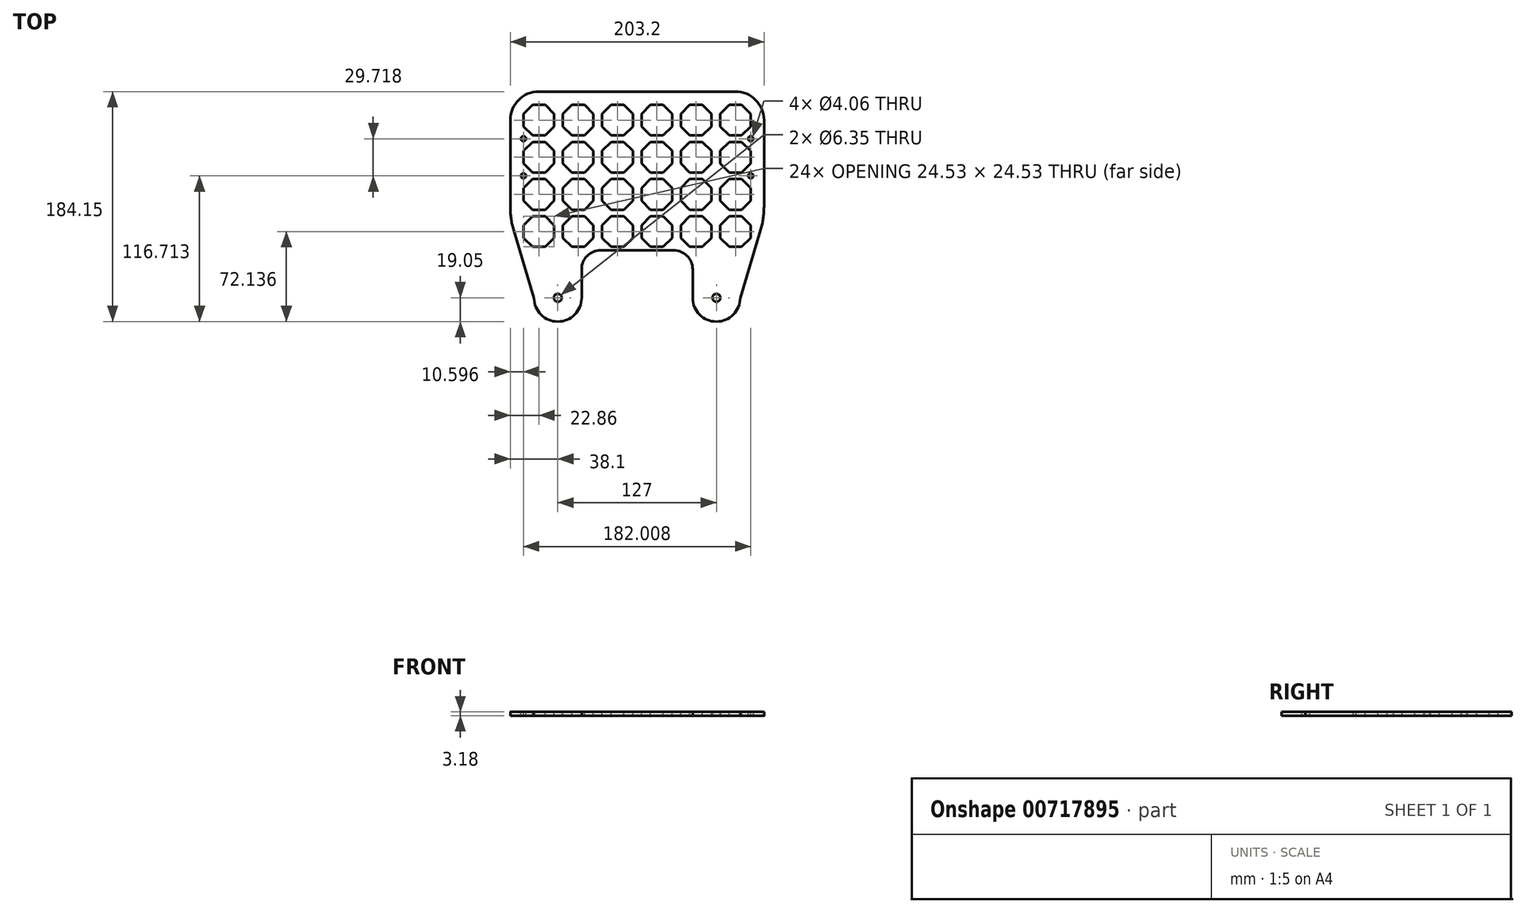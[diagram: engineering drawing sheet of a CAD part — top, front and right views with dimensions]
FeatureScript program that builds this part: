
annotation { "Feature Type Name" : "Feature", "Feature Type Description" : "" }
export const myFeature = defineFeature(function(context is Context, id is Id, definition is map)
    precondition{}
    {
        {
            var Q0;
            Q0=qCreatedBy(makeId("Top.planeOp"),FACE);
            var sketch = newSketch(context, id + "F0", { "sketchPlane" : qUnion([Q0])});
            skLineSegment(sketch, "E0.bottom", {"start": v(111.62, -50.8) * mm, "end": v(-91.58, -50.8) * mm});
            skLineSegment(sketch, "E0.top", {"start": v(88.76, 50.8) * mm, "end": v(-68.72, 50.8) * mm});
            skLineSegment(sketch, "E0.left", {"start": v(111.62, -41.48) * mm, "end": v(111.62, 27.94) * mm});
            skLineSegment(sketch, "E0.right", {"start": v(-91.58, -41.48) * mm, "end": v(-91.58, 27.94) * mm});
            skPoint(sketch, "E0.middle", {"position": v(10.02, 0) * mm});
            skLineSegment(sketch, "E1.bottom", {"start": v(-91.58, -50.8) * mm, "end": v(111.62, -50.8) * mm});
            skLineSegment(sketch, "E1.top", {"start": v(-19.19, -76.2) * mm, "end": v(39.23, -76.2) * mm});
            skLineSegment(sketch, "E2.bottom", {"start": v(54.47, -76.2) * mm, "end": v(92.57, -76.2) * mm});
            skLineSegment(sketch, "E2.top", {"start": v(54.47, -114.3) * mm, "end": v(92.57, -114.3) * mm});
            skLineSegment(sketch, "E2.left", {"start": v(54.47, -91.44) * mm, "end": v(54.47, -114.3) * mm});
            skLineSegment(sketch, "E2.right", {"start": v(92.57, -76.2) * mm, "end": v(92.57, -114.3) * mm});
            skPoint(sketch, "E3.oppositeSnap0", {"position": v(73.52, -114.3) * mm});
            skLineSegment(sketch, "E3.bottom", {"start": v(-72.53, -76.2) * mm, "end": v(-34.43, -76.2) * mm});
            skLineSegment(sketch, "E3.top", {"start": v(-72.53, -114.3) * mm, "end": v(-34.43, -114.3) * mm});
            skLineSegment(sketch, "E3.left", {"start": v(-72.53, -76.2) * mm, "end": v(-72.53, -114.3) * mm});
            skLineSegment(sketch, "E3.right", {"start": v(-34.43, -91.44) * mm, "end": v(-34.43, -114.3) * mm});
            skCircle(sketch, "E4", {"center": v(73.52, -114.3) * mm, "radius": 19.05 * mm});
            skCircle(sketch, "E5", {"center": v(-53.48, -114.3) * mm, "radius": 19.05 * mm});
            skLineSegment(sketch, "E6", {"start": v(-88.9, -59.73) * mm, "end": v(-72.53, -114.3) * mm});
            skLineSegment(sketch, "E7", {"start": v(108.94, -59.73) * mm, "end": v(92.57, -114.3) * mm});
            skPoint(sketch, "E1.left.end.orphan", {"position": v(-91.58, -76.2) * mm});
            skPoint(sketch, "E8.orphan", {"position": v(111.62, -76.2) * mm});
            skPoint(sketch, "E9.visualSharp", {"position": v(-91.58, 50.8) * mm});
            skArc(sketch, "E9.filletArc", {"start": v(-68.72, 50.8) * mm, "mid": v(-84.88, 44.1) * mm, "end": v(-91.58, 27.94) * mm});
            skPoint(sketch, "E10.visualSharp", {"position": v(111.62, 50.8) * mm});
            skArc(sketch, "E10.filletArc", {"start": v(111.62, 27.94) * mm, "mid": v(104.92, 44.1) * mm, "end": v(88.76, 50.8) * mm});
            skPoint(sketch, "E11.visualSharp", {"position": v(-91.58, -50.8) * mm});
            skArc(sketch, "E11.filletArc", {"start": v(-91.58, -41.48) * mm, "mid": v(-90.9, -50.7) * mm, "end": v(-88.9, -59.73) * mm});
            skPoint(sketch, "E12.visualSharp", {"position": v(111.62, -50.8) * mm});
            skArc(sketch, "E12.filletArc", {"start": v(108.94, -59.73) * mm, "mid": v(110.95, -50.7) * mm, "end": v(111.62, -41.48) * mm});
            skCircle(sketch, "E13", {"center": v(-53.48, -114.3) * mm, "radius": 3.18 * mm});
            skCircle(sketch, "E14", {"center": v(73.52, -114.3) * mm, "radius": 3.18 * mm});
            skPoint(sketch, "E15.newPointA", {"position": v(-34.43, -76.2) * mm});
            skArc(sketch, "E15.filletArc", {"start": v(-19.19, -76.2) * mm, "mid": v(-29.97, -80.66) * mm, "end": v(-34.43, -91.44) * mm});
            skPoint(sketch, "E16.newPointB", {"position": v(54.47, -76.2) * mm});
            skArc(sketch, "E16.filletArc", {"start": v(54.47, -91.44) * mm, "mid": v(50, -80.66) * mm, "end": v(39.23, -76.2) * mm});
            skSolve(sketch);
        }
        {
            var Q0;
            Q0=qSketchRegion(id+"F0",true);
            extrude(context, id + "F1", {"entities" : qUnion([Q0]), "depth" : 3.17 * mm, "offsetDistance" : 25.4 * mm});
        }
        {
            var Q0;
            Q0=makeQuery(id+"F1.opExtrude","CAP_FACE",FACE,{"disambiguationData":[OSD([sQuery(id+"F0.wireOp",EDGE,"E0.top"),sQuery(id+"F0.wireOp",EDGE,"E0.left"),sQuery(id+"F0.wireOp",EDGE,"E0.right"),sQuery(id+"F0.wireOp",EDGE,"E1.top"),sQuery(id+"F0.wireOp",EDGE,"E2.left"),sQuery(id+"F0.wireOp",EDGE,"E3.right"),sQuery(id+"F0.wireOp",EDGE,"E4"),sQuery(id+"F0.wireOp",EDGE,"E5"),sQuery(id+"F0.wireOp",EDGE,"E6"),sQuery(id+"F0.wireOp",EDGE,"E7"),sQuery(id+"F0.wireOp",EDGE,"E9.filletArc"),sQuery(id+"F0.wireOp",EDGE,"E10.filletArc"),sQuery(id+"F0.wireOp",EDGE,"E11.filletArc"),sQuery(id+"F0.wireOp",EDGE,"E12.filletArc"),sQuery(id+"F0.wireOp",EDGE,"E13"),sQuery(id+"F0.wireOp",EDGE,"E14"),sQuery(id+"F0.wireOp",EDGE,"E15.filletArc"),sQuery(id+"F0.wireOp",EDGE,"E16.filletArc")])],"isStart":false});
            var sketch = newSketch(context, id + "F2", { "sketchPlane" : qUnion([Q0])});
            skCircle(sketch, "E17.cCircle", {"center": v(-68.72, 27.94) * mm, "radius": 12.26 * mm, "construction": true});
            skLineSegment(sketch, "E17.0", {"start": v(-73.8, 40.2) * mm, "end": v(-63.64, 40.2) * mm});
            skLineSegment(sketch, "E17.1", {"start": v(-63.64, 40.2) * mm, "end": v(-56.46, 33.02) * mm});
            skLineSegment(sketch, "E17.2", {"start": v(-56.46, 33.02) * mm, "end": v(-56.46, 22.86) * mm});
            skLineSegment(sketch, "E17.3", {"start": v(-56.46, 22.86) * mm, "end": v(-63.64, 15.68) * mm});
            skLineSegment(sketch, "E17.4", {"start": v(-63.64, 15.68) * mm, "end": v(-73.8, 15.68) * mm});
            skLineSegment(sketch, "E17.5", {"start": v(-73.8, 15.68) * mm, "end": v(-80.98, 22.86) * mm});
            skLineSegment(sketch, "E17.6", {"start": v(-80.98, 22.86) * mm, "end": v(-80.98, 33.02) * mm});
            skLineSegment(sketch, "E17.7", {"start": v(-80.98, 33.02) * mm, "end": v(-73.8, 40.2) * mm});
            skPoint(sketch, "E17.0.midPoint", {"position": v(-68.72, 40.2) * mm});
            skLineSegment(sketch, "E18", {"start": v(10.02, 50.8) * mm, "end": v(10.02, -76.2) * mm, "construction": true});
            skLineSegment(sketch, "E19.0.1.0", {"start": v(-63.64, -14.04) * mm, "end": v(-73.8, -14.04) * mm});
            skLineSegment(sketch, "E19.0.1.1", {"start": v(-73.8, -14.04) * mm, "end": v(-80.98, -6.86) * mm});
            skLineSegment(sketch, "E19.0.1.2", {"start": v(-80.98, -6.86) * mm, "end": v(-80.98, 3.3) * mm});
            skLineSegment(sketch, "E19.0.1.3", {"start": v(-80.98, 3.3) * mm, "end": v(-73.8, 10.49) * mm});
            skLineSegment(sketch, "E19.0.1.4", {"start": v(-73.8, 10.49) * mm, "end": v(-63.64, 10.49) * mm});
            skLineSegment(sketch, "E19.0.1.5", {"start": v(-63.64, 10.49) * mm, "end": v(-56.46, 3.3) * mm});
            skLineSegment(sketch, "E19.0.1.6", {"start": v(-56.46, 3.3) * mm, "end": v(-56.46, -6.86) * mm});
            skLineSegment(sketch, "E19.0.1.7", {"start": v(-56.46, -6.86) * mm, "end": v(-63.64, -14.04) * mm});
            skLineSegment(sketch, "E19.0.2.0", {"start": v(-63.64, -43.76) * mm, "end": v(-73.8, -43.76) * mm});
            skLineSegment(sketch, "E19.0.2.1", {"start": v(-73.8, -43.76) * mm, "end": v(-80.98, -36.58) * mm});
            skLineSegment(sketch, "E19.0.2.2", {"start": v(-80.98, -36.58) * mm, "end": v(-80.98, -26.42) * mm});
            skLineSegment(sketch, "E19.0.2.3", {"start": v(-80.98, -26.42) * mm, "end": v(-73.8, -19.23) * mm});
            skLineSegment(sketch, "E19.0.2.4", {"start": v(-73.8, -19.23) * mm, "end": v(-63.64, -19.23) * mm});
            skLineSegment(sketch, "E19.0.2.5", {"start": v(-63.64, -19.23) * mm, "end": v(-56.46, -26.42) * mm});
            skLineSegment(sketch, "E19.0.2.6", {"start": v(-56.46, -26.42) * mm, "end": v(-56.46, -36.58) * mm});
            skLineSegment(sketch, "E19.0.2.7", {"start": v(-56.46, -36.58) * mm, "end": v(-63.64, -43.76) * mm});
            skLineSegment(sketch, "E19.0.3.0", {"start": v(-63.64, -73.48) * mm, "end": v(-73.8, -73.48) * mm});
            skLineSegment(sketch, "E19.0.3.1", {"start": v(-73.8, -73.48) * mm, "end": v(-80.98, -66.3) * mm});
            skLineSegment(sketch, "E19.0.3.2", {"start": v(-80.98, -66.3) * mm, "end": v(-80.98, -56.13) * mm});
            skLineSegment(sketch, "E19.0.3.3", {"start": v(-80.98, -56.13) * mm, "end": v(-73.8, -48.95) * mm});
            skLineSegment(sketch, "E19.0.3.4", {"start": v(-73.8, -48.95) * mm, "end": v(-63.64, -48.95) * mm});
            skLineSegment(sketch, "E19.0.3.5", {"start": v(-63.64, -48.95) * mm, "end": v(-56.46, -56.13) * mm});
            skLineSegment(sketch, "E19.0.3.6", {"start": v(-56.46, -56.13) * mm, "end": v(-56.46, -66.3) * mm});
            skLineSegment(sketch, "E19.0.3.7", {"start": v(-56.46, -66.3) * mm, "end": v(-63.64, -73.48) * mm});
            skLineSegment(sketch, "E19.1.0.0", {"start": v(-32.14, 15.68) * mm, "end": v(-42.3, 15.68) * mm});
            skLineSegment(sketch, "E19.1.0.1", {"start": v(-42.3, 15.68) * mm, "end": v(-49.49, 22.86) * mm});
            skLineSegment(sketch, "E19.1.0.2", {"start": v(-49.49, 22.86) * mm, "end": v(-49.49, 33.02) * mm});
            skLineSegment(sketch, "E19.1.0.3", {"start": v(-49.49, 33.02) * mm, "end": v(-42.3, 40.2) * mm});
            skLineSegment(sketch, "E19.1.0.4", {"start": v(-42.3, 40.2) * mm, "end": v(-32.14, 40.2) * mm});
            skLineSegment(sketch, "E19.1.0.5", {"start": v(-32.14, 40.2) * mm, "end": v(-24.96, 33.02) * mm});
            skLineSegment(sketch, "E19.1.0.6", {"start": v(-24.96, 33.02) * mm, "end": v(-24.96, 22.86) * mm});
            skLineSegment(sketch, "E19.1.0.7", {"start": v(-24.96, 22.86) * mm, "end": v(-32.14, 15.68) * mm});
            skLineSegment(sketch, "E19.1.1.0", {"start": v(-32.14, -14.04) * mm, "end": v(-42.3, -14.04) * mm});
            skLineSegment(sketch, "E19.1.1.1", {"start": v(-42.3, -14.04) * mm, "end": v(-49.49, -6.86) * mm});
            skLineSegment(sketch, "E19.1.1.2", {"start": v(-49.49, -6.86) * mm, "end": v(-49.49, 3.3) * mm});
            skLineSegment(sketch, "E19.1.1.3", {"start": v(-49.49, 3.3) * mm, "end": v(-42.3, 10.49) * mm});
            skLineSegment(sketch, "E19.1.1.4", {"start": v(-42.3, 10.49) * mm, "end": v(-32.14, 10.49) * mm});
            skLineSegment(sketch, "E19.1.1.5", {"start": v(-32.14, 10.49) * mm, "end": v(-24.96, 3.3) * mm});
            skLineSegment(sketch, "E19.1.1.6", {"start": v(-24.96, 3.3) * mm, "end": v(-24.96, -6.86) * mm});
            skLineSegment(sketch, "E19.1.1.7", {"start": v(-24.96, -6.86) * mm, "end": v(-32.14, -14.04) * mm});
            skLineSegment(sketch, "E19.1.2.0", {"start": v(-32.14, -43.76) * mm, "end": v(-42.3, -43.76) * mm});
            skLineSegment(sketch, "E19.1.2.1", {"start": v(-42.3, -43.76) * mm, "end": v(-49.49, -36.58) * mm});
            skLineSegment(sketch, "E19.1.2.2", {"start": v(-49.49, -36.58) * mm, "end": v(-49.49, -26.42) * mm});
            skLineSegment(sketch, "E19.1.2.3", {"start": v(-49.49, -26.42) * mm, "end": v(-42.3, -19.23) * mm});
            skLineSegment(sketch, "E19.1.2.4", {"start": v(-42.3, -19.23) * mm, "end": v(-32.14, -19.23) * mm});
            skLineSegment(sketch, "E19.1.2.5", {"start": v(-32.14, -19.23) * mm, "end": v(-24.96, -26.42) * mm});
            skLineSegment(sketch, "E19.1.2.6", {"start": v(-24.96, -26.42) * mm, "end": v(-24.96, -36.58) * mm});
            skLineSegment(sketch, "E19.1.2.7", {"start": v(-24.96, -36.58) * mm, "end": v(-32.14, -43.76) * mm});
            skLineSegment(sketch, "E19.1.3.0", {"start": v(-32.14, -73.48) * mm, "end": v(-42.3, -73.48) * mm});
            skLineSegment(sketch, "E19.1.3.1", {"start": v(-42.3, -73.48) * mm, "end": v(-49.49, -66.3) * mm});
            skLineSegment(sketch, "E19.1.3.2", {"start": v(-49.49, -66.3) * mm, "end": v(-49.49, -56.13) * mm});
            skLineSegment(sketch, "E19.1.3.3", {"start": v(-49.49, -56.13) * mm, "end": v(-42.3, -48.95) * mm});
            skLineSegment(sketch, "E19.1.3.4", {"start": v(-42.3, -48.95) * mm, "end": v(-32.14, -48.95) * mm});
            skLineSegment(sketch, "E19.1.3.5", {"start": v(-32.14, -48.95) * mm, "end": v(-24.96, -56.13) * mm});
            skLineSegment(sketch, "E19.1.3.6", {"start": v(-24.96, -56.13) * mm, "end": v(-24.96, -66.3) * mm});
            skLineSegment(sketch, "E19.1.3.7", {"start": v(-24.96, -66.3) * mm, "end": v(-32.14, -73.48) * mm});
            skLineSegment(sketch, "E19.2.0.0", {"start": v(-0.65, 15.68) * mm, "end": v(-10.8, 15.68) * mm});
            skLineSegment(sketch, "E19.2.0.1", {"start": v(-10.8, 15.68) * mm, "end": v(-18, 22.86) * mm});
            skLineSegment(sketch, "E19.2.0.2", {"start": v(-18, 22.86) * mm, "end": v(-18, 33.02) * mm});
            skLineSegment(sketch, "E19.2.0.3", {"start": v(-18, 33.02) * mm, "end": v(-10.8, 40.2) * mm});
            skLineSegment(sketch, "E19.2.0.4", {"start": v(-10.8, 40.2) * mm, "end": v(-0.65, 40.2) * mm});
            skLineSegment(sketch, "E19.2.0.5", {"start": v(-0.65, 40.2) * mm, "end": v(6.54, 33.02) * mm});
            skLineSegment(sketch, "E19.2.0.6", {"start": v(6.54, 33.02) * mm, "end": v(6.54, 22.86) * mm});
            skLineSegment(sketch, "E19.2.0.7", {"start": v(6.54, 22.86) * mm, "end": v(-0.65, 15.68) * mm});
            skLineSegment(sketch, "E19.2.1.0", {"start": v(-0.65, -14.04) * mm, "end": v(-10.8, -14.04) * mm});
            skLineSegment(sketch, "E19.2.1.1", {"start": v(-10.8, -14.04) * mm, "end": v(-18, -6.86) * mm});
            skLineSegment(sketch, "E19.2.1.2", {"start": v(-18, -6.86) * mm, "end": v(-18, 3.3) * mm});
            skLineSegment(sketch, "E19.2.1.3", {"start": v(-18, 3.3) * mm, "end": v(-10.8, 10.49) * mm});
            skLineSegment(sketch, "E19.2.1.4", {"start": v(-10.8, 10.49) * mm, "end": v(-0.65, 10.49) * mm});
            skLineSegment(sketch, "E19.2.1.5", {"start": v(-0.65, 10.49) * mm, "end": v(6.54, 3.3) * mm});
            skLineSegment(sketch, "E19.2.1.6", {"start": v(6.54, 3.3) * mm, "end": v(6.54, -6.86) * mm});
            skLineSegment(sketch, "E19.2.1.7", {"start": v(6.54, -6.86) * mm, "end": v(-0.65, -14.04) * mm});
            skLineSegment(sketch, "E19.2.2.0", {"start": v(-0.65, -43.76) * mm, "end": v(-10.8, -43.76) * mm});
            skLineSegment(sketch, "E19.2.2.1", {"start": v(-10.8, -43.76) * mm, "end": v(-18, -36.58) * mm});
            skLineSegment(sketch, "E19.2.2.2", {"start": v(-18, -36.58) * mm, "end": v(-18, -26.42) * mm});
            skLineSegment(sketch, "E19.2.2.3", {"start": v(-18, -26.42) * mm, "end": v(-10.8, -19.23) * mm});
            skLineSegment(sketch, "E19.2.2.4", {"start": v(-10.8, -19.23) * mm, "end": v(-0.65, -19.23) * mm});
            skLineSegment(sketch, "E19.2.2.5", {"start": v(-0.65, -19.23) * mm, "end": v(6.54, -26.42) * mm});
            skLineSegment(sketch, "E19.2.2.6", {"start": v(6.54, -26.42) * mm, "end": v(6.54, -36.58) * mm});
            skLineSegment(sketch, "E19.2.2.7", {"start": v(6.54, -36.58) * mm, "end": v(-0.65, -43.76) * mm});
            skLineSegment(sketch, "E19.2.3.0", {"start": v(-0.65, -73.48) * mm, "end": v(-10.8, -73.48) * mm});
            skLineSegment(sketch, "E19.2.3.1", {"start": v(-10.8, -73.48) * mm, "end": v(-18, -66.3) * mm});
            skLineSegment(sketch, "E19.2.3.2", {"start": v(-18, -66.3) * mm, "end": v(-18, -56.13) * mm});
            skLineSegment(sketch, "E19.2.3.3", {"start": v(-18, -56.13) * mm, "end": v(-10.8, -48.95) * mm});
            skLineSegment(sketch, "E19.2.3.4", {"start": v(-10.8, -48.95) * mm, "end": v(-0.65, -48.95) * mm});
            skLineSegment(sketch, "E19.2.3.5", {"start": v(-0.65, -48.95) * mm, "end": v(6.54, -56.13) * mm});
            skLineSegment(sketch, "E19.2.3.6", {"start": v(6.54, -56.13) * mm, "end": v(6.54, -66.3) * mm});
            skLineSegment(sketch, "E19.2.3.7", {"start": v(6.54, -66.3) * mm, "end": v(-0.65, -73.48) * mm});
            skLineSegment(sketch, "E19.direction1", {"start": v(-73.8, 15.68) * mm, "end": v(-42.3, 15.68) * mm, "construction": true});
            skLineSegment(sketch, "E19.direction2", {"start": v(-73.8, 15.68) * mm, "end": v(-73.8, -14.04) * mm, "construction": true});
            skLineSegment(sketch, "E20.0.3.0", {"start": v(30.85, 15.68) * mm, "end": v(20.69, 15.68) * mm});
            skLineSegment(sketch, "E20.3.3.0", {"start": v(20.69, 15.68) * mm, "end": v(13.5, 22.86) * mm});
            skLineSegment(sketch, "E20.6.3.0", {"start": v(13.5, 22.86) * mm, "end": v(13.5, 33.02) * mm});
            skLineSegment(sketch, "E20.9.3.0", {"start": v(13.5, 33.02) * mm, "end": v(20.69, 40.2) * mm});
            skLineSegment(sketch, "E20.12.3.0", {"start": v(20.69, 40.2) * mm, "end": v(30.85, 40.2) * mm});
            skLineSegment(sketch, "E20.15.3.0", {"start": v(30.85, 40.2) * mm, "end": v(38.03, 33.02) * mm});
            skLineSegment(sketch, "E20.18.3.0", {"start": v(38.03, 33.02) * mm, "end": v(38.03, 22.86) * mm});
            skLineSegment(sketch, "E20.21.3.0", {"start": v(38.03, 22.86) * mm, "end": v(30.85, 15.68) * mm});
            skLineSegment(sketch, "E20.0.3.1", {"start": v(30.85, -14.04) * mm, "end": v(20.69, -14.04) * mm});
            skLineSegment(sketch, "E20.3.3.1", {"start": v(20.69, -14.04) * mm, "end": v(13.5, -6.86) * mm});
            skLineSegment(sketch, "E20.6.3.1", {"start": v(13.5, -6.86) * mm, "end": v(13.5, 3.3) * mm});
            skLineSegment(sketch, "E20.9.3.1", {"start": v(13.5, 3.3) * mm, "end": v(20.69, 10.49) * mm});
            skLineSegment(sketch, "E20.12.3.1", {"start": v(20.69, 10.49) * mm, "end": v(30.85, 10.49) * mm});
            skLineSegment(sketch, "E20.15.3.1", {"start": v(30.85, 10.49) * mm, "end": v(38.03, 3.3) * mm});
            skLineSegment(sketch, "E20.18.3.1", {"start": v(38.03, 3.3) * mm, "end": v(38.03, -6.86) * mm});
            skLineSegment(sketch, "E20.21.3.1", {"start": v(38.03, -6.86) * mm, "end": v(30.85, -14.04) * mm});
            skLineSegment(sketch, "E20.0.3.2", {"start": v(30.85, -43.76) * mm, "end": v(20.69, -43.76) * mm});
            skLineSegment(sketch, "E20.3.3.2", {"start": v(20.69, -43.76) * mm, "end": v(13.5, -36.58) * mm});
            skLineSegment(sketch, "E20.6.3.2", {"start": v(13.5, -36.58) * mm, "end": v(13.5, -26.42) * mm});
            skLineSegment(sketch, "E20.9.3.2", {"start": v(13.5, -26.42) * mm, "end": v(20.69, -19.23) * mm});
            skLineSegment(sketch, "E20.12.3.2", {"start": v(20.69, -19.23) * mm, "end": v(30.85, -19.23) * mm});
            skLineSegment(sketch, "E20.15.3.2", {"start": v(30.85, -19.23) * mm, "end": v(38.03, -26.42) * mm});
            skLineSegment(sketch, "E20.18.3.2", {"start": v(38.03, -26.42) * mm, "end": v(38.03, -36.58) * mm});
            skLineSegment(sketch, "E20.21.3.2", {"start": v(38.03, -36.58) * mm, "end": v(30.85, -43.76) * mm});
            skLineSegment(sketch, "E20.0.3.3", {"start": v(30.85, -73.48) * mm, "end": v(20.69, -73.48) * mm});
            skLineSegment(sketch, "E20.3.3.3", {"start": v(20.69, -73.48) * mm, "end": v(13.5, -66.3) * mm});
            skLineSegment(sketch, "E20.6.3.3", {"start": v(13.5, -66.3) * mm, "end": v(13.5, -56.13) * mm});
            skLineSegment(sketch, "E20.9.3.3", {"start": v(13.5, -56.13) * mm, "end": v(20.69, -48.95) * mm});
            skLineSegment(sketch, "E20.12.3.3", {"start": v(20.69, -48.95) * mm, "end": v(30.85, -48.95) * mm});
            skLineSegment(sketch, "E20.15.3.3", {"start": v(30.85, -48.95) * mm, "end": v(38.03, -56.13) * mm});
            skLineSegment(sketch, "E20.18.3.3", {"start": v(38.03, -56.13) * mm, "end": v(38.03, -66.3) * mm});
            skLineSegment(sketch, "E20.21.3.3", {"start": v(38.03, -66.3) * mm, "end": v(30.85, -73.48) * mm});
            skLineSegment(sketch, "E20.0.4.0", {"start": v(62.34, 15.68) * mm, "end": v(52.18, 15.68) * mm});
            skLineSegment(sketch, "E20.3.4.0", {"start": v(52.18, 15.68) * mm, "end": v(45, 22.86) * mm});
            skLineSegment(sketch, "E20.6.4.0", {"start": v(45, 22.86) * mm, "end": v(45, 33.02) * mm});
            skLineSegment(sketch, "E20.9.4.0", {"start": v(45, 33.02) * mm, "end": v(52.18, 40.2) * mm});
            skLineSegment(sketch, "E20.12.4.0", {"start": v(52.18, 40.2) * mm, "end": v(62.34, 40.2) * mm});
            skLineSegment(sketch, "E20.15.4.0", {"start": v(62.34, 40.2) * mm, "end": v(69.53, 33.02) * mm});
            skLineSegment(sketch, "E20.18.4.0", {"start": v(69.53, 33.02) * mm, "end": v(69.53, 22.86) * mm});
            skLineSegment(sketch, "E20.21.4.0", {"start": v(69.53, 22.86) * mm, "end": v(62.34, 15.68) * mm});
            skLineSegment(sketch, "E20.0.4.1", {"start": v(62.34, -14.04) * mm, "end": v(52.18, -14.04) * mm});
            skLineSegment(sketch, "E20.3.4.1", {"start": v(52.18, -14.04) * mm, "end": v(45, -6.86) * mm});
            skLineSegment(sketch, "E20.6.4.1", {"start": v(45, -6.86) * mm, "end": v(45, 3.3) * mm});
            skLineSegment(sketch, "E20.9.4.1", {"start": v(45, 3.3) * mm, "end": v(52.18, 10.49) * mm});
            skLineSegment(sketch, "E20.12.4.1", {"start": v(52.18, 10.49) * mm, "end": v(62.34, 10.49) * mm});
            skLineSegment(sketch, "E20.15.4.1", {"start": v(62.34, 10.49) * mm, "end": v(69.53, 3.3) * mm});
            skLineSegment(sketch, "E20.18.4.1", {"start": v(69.53, 3.3) * mm, "end": v(69.53, -6.86) * mm});
            skLineSegment(sketch, "E20.21.4.1", {"start": v(69.53, -6.86) * mm, "end": v(62.34, -14.04) * mm});
            skLineSegment(sketch, "E20.0.4.2", {"start": v(62.34, -43.76) * mm, "end": v(52.18, -43.76) * mm});
            skLineSegment(sketch, "E20.3.4.2", {"start": v(52.18, -43.76) * mm, "end": v(45, -36.58) * mm});
            skLineSegment(sketch, "E20.6.4.2", {"start": v(45, -36.58) * mm, "end": v(45, -26.42) * mm});
            skLineSegment(sketch, "E20.9.4.2", {"start": v(45, -26.42) * mm, "end": v(52.18, -19.23) * mm});
            skLineSegment(sketch, "E20.12.4.2", {"start": v(52.18, -19.23) * mm, "end": v(62.34, -19.23) * mm});
            skLineSegment(sketch, "E20.15.4.2", {"start": v(62.34, -19.23) * mm, "end": v(69.53, -26.42) * mm});
            skLineSegment(sketch, "E20.18.4.2", {"start": v(69.53, -26.42) * mm, "end": v(69.53, -36.58) * mm});
            skLineSegment(sketch, "E20.21.4.2", {"start": v(69.53, -36.58) * mm, "end": v(62.34, -43.76) * mm});
            skLineSegment(sketch, "E20.0.4.3", {"start": v(62.34, -73.48) * mm, "end": v(52.18, -73.48) * mm});
            skLineSegment(sketch, "E20.3.4.3", {"start": v(52.18, -73.48) * mm, "end": v(45, -66.3) * mm});
            skLineSegment(sketch, "E20.6.4.3", {"start": v(45, -66.3) * mm, "end": v(45, -56.13) * mm});
            skLineSegment(sketch, "E20.9.4.3", {"start": v(45, -56.13) * mm, "end": v(52.18, -48.95) * mm});
            skLineSegment(sketch, "E20.12.4.3", {"start": v(52.18, -48.95) * mm, "end": v(62.34, -48.95) * mm});
            skLineSegment(sketch, "E20.15.4.3", {"start": v(62.34, -48.95) * mm, "end": v(69.53, -56.13) * mm});
            skLineSegment(sketch, "E20.18.4.3", {"start": v(69.53, -56.13) * mm, "end": v(69.53, -66.3) * mm});
            skLineSegment(sketch, "E20.21.4.3", {"start": v(69.53, -66.3) * mm, "end": v(62.34, -73.48) * mm});
            skLineSegment(sketch, "E20.0.5.0", {"start": v(93.84, 15.68) * mm, "end": v(83.68, 15.68) * mm});
            skLineSegment(sketch, "E20.3.5.0", {"start": v(83.68, 15.68) * mm, "end": v(76.5, 22.86) * mm});
            skLineSegment(sketch, "E20.6.5.0", {"start": v(76.5, 22.86) * mm, "end": v(76.5, 33.02) * mm});
            skLineSegment(sketch, "E20.9.5.0", {"start": v(76.5, 33.02) * mm, "end": v(83.68, 40.2) * mm});
            skLineSegment(sketch, "E20.12.5.0", {"start": v(83.68, 40.2) * mm, "end": v(93.84, 40.2) * mm});
            skLineSegment(sketch, "E20.15.5.0", {"start": v(93.84, 40.2) * mm, "end": v(101.02, 33.02) * mm});
            skLineSegment(sketch, "E20.18.5.0", {"start": v(101.02, 33.02) * mm, "end": v(101.02, 22.86) * mm});
            skLineSegment(sketch, "E20.21.5.0", {"start": v(101.02, 22.86) * mm, "end": v(93.84, 15.68) * mm});
            skLineSegment(sketch, "E20.0.5.1", {"start": v(93.84, -14.04) * mm, "end": v(83.68, -14.04) * mm});
            skLineSegment(sketch, "E20.3.5.1", {"start": v(83.68, -14.04) * mm, "end": v(76.5, -6.86) * mm});
            skLineSegment(sketch, "E20.6.5.1", {"start": v(76.5, -6.86) * mm, "end": v(76.5, 3.3) * mm});
            skLineSegment(sketch, "E20.9.5.1", {"start": v(76.5, 3.3) * mm, "end": v(83.68, 10.49) * mm});
            skLineSegment(sketch, "E20.12.5.1", {"start": v(83.68, 10.49) * mm, "end": v(93.84, 10.49) * mm});
            skLineSegment(sketch, "E20.15.5.1", {"start": v(93.84, 10.49) * mm, "end": v(101.02, 3.3) * mm});
            skLineSegment(sketch, "E20.18.5.1", {"start": v(101.02, 3.3) * mm, "end": v(101.02, -6.86) * mm});
            skLineSegment(sketch, "E20.21.5.1", {"start": v(101.02, -6.86) * mm, "end": v(93.84, -14.04) * mm});
            skLineSegment(sketch, "E20.0.5.2", {"start": v(93.84, -43.76) * mm, "end": v(83.68, -43.76) * mm});
            skLineSegment(sketch, "E20.3.5.2", {"start": v(83.68, -43.76) * mm, "end": v(76.5, -36.58) * mm});
            skLineSegment(sketch, "E20.6.5.2", {"start": v(76.5, -36.58) * mm, "end": v(76.5, -26.42) * mm});
            skLineSegment(sketch, "E20.9.5.2", {"start": v(76.5, -26.42) * mm, "end": v(83.68, -19.23) * mm});
            skLineSegment(sketch, "E20.12.5.2", {"start": v(83.68, -19.23) * mm, "end": v(93.84, -19.23) * mm});
            skLineSegment(sketch, "E20.15.5.2", {"start": v(93.84, -19.23) * mm, "end": v(101.02, -26.42) * mm});
            skLineSegment(sketch, "E20.18.5.2", {"start": v(101.02, -26.42) * mm, "end": v(101.02, -36.58) * mm});
            skLineSegment(sketch, "E20.21.5.2", {"start": v(101.02, -36.58) * mm, "end": v(93.84, -43.76) * mm});
            skLineSegment(sketch, "E20.0.5.3", {"start": v(93.84, -73.48) * mm, "end": v(83.68, -73.48) * mm});
            skLineSegment(sketch, "E20.3.5.3", {"start": v(83.68, -73.48) * mm, "end": v(76.5, -66.3) * mm});
            skLineSegment(sketch, "E20.6.5.3", {"start": v(76.5, -66.3) * mm, "end": v(76.5, -56.13) * mm});
            skLineSegment(sketch, "E20.9.5.3", {"start": v(76.5, -56.13) * mm, "end": v(83.68, -48.95) * mm});
            skLineSegment(sketch, "E20.12.5.3", {"start": v(83.68, -48.95) * mm, "end": v(93.84, -48.95) * mm});
            skLineSegment(sketch, "E20.15.5.3", {"start": v(93.84, -48.95) * mm, "end": v(101.02, -56.13) * mm});
            skLineSegment(sketch, "E20.18.5.3", {"start": v(101.02, -56.13) * mm, "end": v(101.02, -66.3) * mm});
            skLineSegment(sketch, "E20.21.5.3", {"start": v(101.02, -66.3) * mm, "end": v(93.84, -73.48) * mm});
            skLineSegment(sketch, "E21", {"start": v(-80.98, 22.86) * mm, "end": v(-80.98, 3.3) * mm, "construction": true});
            skCircle(sketch, "E22", {"center": v(-80.98, 13.08) * mm, "radius": 2.03 * mm});
            skLineSegment(sketch, "E23", {"start": v(-80.98, -6.86) * mm, "end": v(-80.98, -26.42) * mm, "construction": true});
            skCircle(sketch, "E24", {"center": v(-80.98, -16.64) * mm, "radius": 2.03 * mm});
            skCircle(sketch, "E25.MirrorC", {"center": v(101.02, 13.08) * mm, "radius": 2.03 * mm});
            skCircle(sketch, "E26.MirrorC", {"center": v(101.02, -16.64) * mm, "radius": 2.03 * mm});
            skSolve(sketch);
        }
        {
            var Q0;
            Q0=qSketchRegion(id+"F2",true);
            extrude(context, id + "F3", {"entities" : qUnion([Q0]), "operationType" : NewBodyOperationType.REMOVE, "endBound" : BoundingType.THROUGH_ALL, "oppositeDirection" : true, "depth" : 25.4 * mm, "offsetDistance" : 25.4 * mm});
        }
    });
